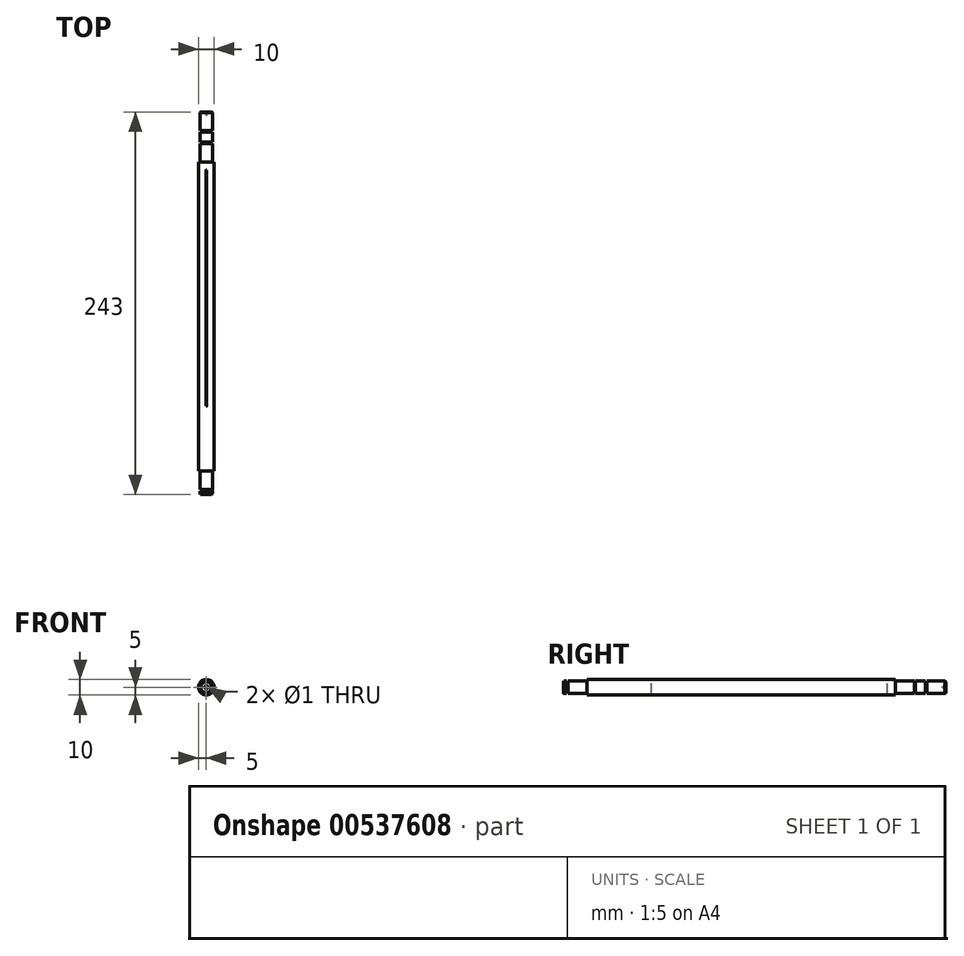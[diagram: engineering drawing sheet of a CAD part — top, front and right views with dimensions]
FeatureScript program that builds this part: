
annotation { "Feature Type Name" : "Feature", "Feature Type Description" : "" }
export const myFeature = defineFeature(function(context is Context, id is Id, definition is map)
    precondition{}
    {
        {
            var Q0;
            Q0=qCreatedBy(makeId("Front.planeOp"),FACE);
            var sketch = newSketch(context, id + "F0", { "sketchPlane" : qUnion([Q0])});
            skCircle(sketch, "E0", {"center": v(0, 0) * mm, "radius": 5 * mm});
            skSolve(sketch);
        }
        {
            var Q0;
            Q0=makeQuery(id+"F0.imprint","IMPRINT",FACE,{"disambiguationData":[TD([[makeQuery(id+"F0.imprint","IMPRINT",EDGE,{"derivedFrom":sQuery(id+"F0.wireOp",EDGE,"E0")}),1.0]])]});
            extrude(context, id + "F1", {"entities" : qUnion([Q0]), "flatOperationType" : FlatOperationType.REMOVE, "depth" : 220 * mm, "offsetDistance" : 25 * mm, "domain" : OperationDomain.MODEL});
        }
        {
            var Q0;
            Q0=qCreatedBy(makeId("Right.planeOp"),FACE);
            var sketch = newSketch(context, id + "F2", { "sketchPlane" : qUnion([Q0])});
            skLineSegment(sketch, "E1", {"start": v(0, 5) * mm, "end": v(-12, 5) * mm});
            skLineSegment(sketch, "E2", {"start": v(-12, 5) * mm, "end": v(-12, 4) * mm});
            skLineSegment(sketch, "E3", {"start": v(-12, 4) * mm, "end": v(0, 4) * mm});
            skLineSegment(sketch, "E4", {"start": v(0, 4) * mm, "end": v(0, 5) * mm});
            skLineSegment(sketch, "E5", {"start": v(-220, 5) * mm, "end": v(-208, 5) * mm});
            skLineSegment(sketch, "E6", {"start": v(-208, 5) * mm, "end": v(-208, 4) * mm});
            skLineSegment(sketch, "E7", {"start": v(-208, 4) * mm, "end": v(-220, 4) * mm});
            skLineSegment(sketch, "E8", {"start": v(-220, 4) * mm, "end": v(-220, 5) * mm});
            skSolve(sketch);
        }
        {
            var Q0;
            Q0 = qSketchRegion(id + "F2", true);
            var Q1;
            Q1=makeQuery(id+"F1.opExtrude","SWEPT_FACE",FACE,{"disambiguationData":[OSD([sQuery(id+"F0.wireOp",EDGE,"E0")])]});
            revolve(context, id + "F3", {"operationType" : NewBodyOperationType.REMOVE, "entities" : qUnion([Q0]), "axis" : qUnion([Q1]), "revolveType" : RevolveType.FULL, "oppositeDirection" : true});
        }
        {
            var Q0;
            Q0=qCreatedBy(makeId("Top.planeOp"),FACE);
            var sketch = newSketch(context, id + "F4", { "sketchPlane" : qUnion([Q0])});
            skLineSegment(sketch, "E9.bottom", {"start": v(0.3, -17) * mm, "end": v(-0.3, -17) * mm});
            skLineSegment(sketch, "E9.top", {"start": v(0.3, -167) * mm, "end": v(-0.3, -167) * mm});
            skLineSegment(sketch, "E9.left", {"start": v(0.3, -17) * mm, "end": v(0.3, -167) * mm});
            skLineSegment(sketch, "E9.right", {"start": v(-0.3, -17) * mm, "end": v(-0.3, -167) * mm});
            skSolve(sketch);
        }
        {
            var Q0;
            Q0 = qSketchRegion(id + "F4", true);
            extrude(context, id + "F5", {"entities" : qUnion([Q0]), "operationType" : NewBodyOperationType.REMOVE, "oppositeDirection" : true, "depth" : 25 * mm, "offsetDistance" : 25 * mm, "symmetric" : true});
        }
        {
            var Q0;
            Q0=makeQuery(id+"F1.opExtrude","CAP_FACE",FACE,{"disambiguationData":[OSD([sQuery(id+"F0.wireOp",EDGE,"E0")])],"isStart":false});
            extrude(context, id + "F6", {"entities" : qUnion([Q0]), "operationType" : NewBodyOperationType.ADD, "depth" : 3 * mm, "offsetDistance" : 25 * mm});
        }
        {
            var Q0;
            Q0=makeQuery(id+"F1.opExtrude","CAP_FACE",FACE,{"disambiguationData":[OSD([sQuery(id+"F0.wireOp",EDGE,"E0")])],"isStart":true});
            extrude(context, id + "F7", {"entities" : qUnion([Q0]), "operationType" : NewBodyOperationType.ADD, "depth" : 20 * mm, "offsetDistance" : 25 * mm});
        }
        {
            var Q0;
            Q0=qCreatedBy(makeId("Right.planeOp"),FACE);
            var sketch = newSketch(context, id + "F8", { "sketchPlane" : qUnion([Q0])});
            skLineSegment(sketch, "E10", {"start": v(0, 4) * mm, "end": v(0, 3) * mm});
            skLineSegment(sketch, "E11", {"start": v(0, 3) * mm, "end": v(0.8, 3) * mm});
            skLineSegment(sketch, "E12", {"start": v(0.8, 3) * mm, "end": v(0.8, 4) * mm});
            skLineSegment(sketch, "E13", {"start": v(0.8, 4) * mm, "end": v(0, 4) * mm});
            skLineSegment(sketch, "E14.bottom", {"start": v(-220.8, 4) * mm, "end": v(-220, 4) * mm});
            skLineSegment(sketch, "E14.top", {"start": v(-220.8, 3) * mm, "end": v(-220, 3) * mm});
            skLineSegment(sketch, "E14.left", {"start": v(-220.8, 4) * mm, "end": v(-220.8, 3) * mm});
            skLineSegment(sketch, "E14.right", {"start": v(-220, 4) * mm, "end": v(-220, 3) * mm});
            skLineSegment(sketch, "E15", {"start": v(0, 0) * mm, "end": v(-212.78, 0) * mm});
            skLineSegment(sketch, "E16", {"start": v(7, 3) * mm, "end": v(8, 3) * mm});
            skLineSegment(sketch, "E17", {"start": v(8, 3) * mm, "end": v(8, 4) * mm});
            skLineSegment(sketch, "E18", {"start": v(8, 4) * mm, "end": v(7, 4) * mm});
            skLineSegment(sketch, "E19", {"start": v(7, 4) * mm, "end": v(7, 3) * mm});
            skSolve(sketch);
        }
        {
            var Q0;
            Q0 = qSketchRegion(id + "F8", true);
            var Q1;
            Q1=sQuery(id+"F8.wireOp",EDGE,"E15");
            revolve(context, id + "F9", {"operationType" : NewBodyOperationType.REMOVE, "entities" : qUnion([Q0]), "axis" : qUnion([Q1]), "revolveType" : RevolveType.FULL, "oppositeDirection" : true});
        }
        {
            var Q0;
            Q0=makeQuery(id+"F6.opExtrude","CAP_EDGE",EDGE,{"disambiguationData":[OSD([sQuery(id+"F2.wireOp",EDGE,"E7"),sQuery(id+"F2.wireOp",EDGE,"E8")])],"isStart":false});
            var Q1;
            Q1=makeQuery(id+"F3.boolean.opBoolean","COPY",EDGE,{"derivedFrom":makeQuery(id+"F3.opRevolve","SWEPT_EDGE",EDGE,{"disambiguationData":[OSD([sQuery(id+"F2.wireOp",EDGE,"E5"),sQuery(id+"F2.wireOp",EDGE,"E6")])]})});
            var Q2;
            Q2=makeQuery(id+"F3.boolean.opBoolean","COPY",EDGE,{"derivedFrom":makeQuery(id+"F3.opRevolve","SWEPT_EDGE",EDGE,{"disambiguationData":[OSD([sQuery(id+"F2.wireOp",EDGE,"E1"),sQuery(id+"F2.wireOp",EDGE,"E2")])]})});
            var Q3;
            Q3=makeQuery(id+"F9.boolean.opBoolean","COPY",EDGE,{"derivedFrom":makeQuery(id+"F9.opRevolve","SWEPT_EDGE",EDGE,{"disambiguationData":[OSD([sQuery(id+"F8.wireOp",EDGE,"E17"),sQuery(id+"F8.wireOp",EDGE,"E18")])]})});
            var Q4;
            Q4=makeQuery(id+"F7.opExtrude","CAP_EDGE",EDGE,{"disambiguationData":[OSD([sQuery(id+"F2.wireOp",EDGE,"E3"),sQuery(id+"F2.wireOp",EDGE,"E4")])],"isStart":false});
            chamfer(context, id + "F10", {"entities" : qUnion([Q0, Q1, Q2, Q3, Q4]), "width" : .5 * mm, "tangentPropagation" : true});
        }
        {
            var Q0;
            Q0=makeQuery(id+"F7.opExtrude","CAP_FACE",FACE,{"disambiguationData":[OSD([sQuery(id+"F0.wireOp",EDGE,"E0")])],"isStart":false});
            var sketch = newSketch(context, id + "F11", { "sketchPlane" : qUnion([Q0])});
            skPoint(sketch, "E20", {"position": v(0, 0) * mm});
            skSolve(sketch);
        }
        {
            var Q0;
            Q0=makeQuery(id+"F6.opExtrude","CAP_FACE",FACE,{"disambiguationData":[OSD([sQuery(id+"F0.wireOp",EDGE,"E0")])],"isStart":false});
            var sketch = newSketch(context, id + "F12", { "sketchPlane" : qUnion([Q0])});
            skPoint(sketch, "E21", {"position": v(0, 0) * mm});
            skSolve(sketch);
        }
        {
            var Q0;
            Q0=sQuery(id+"F12.wireOp",VERTEX,"E21");
            var Q1;
            Q1=sQuery(id+"F11.wireOp",VERTEX,"E20");
            var Q2;
            Q2=makeQuery(id+"F1.opExtrude","SWEPT_BODY",BODY,{"disambiguationData":[OSD([sQuery(id+"F0.wireOp",EDGE,"E0")])]});
            hole(context, id + "F13", {"style" : HoleStyle.C_SINK, "endStyle" : HoleEndStyle.BLIND, "holeDiameter" : 1 * mm, "cSinkDiameter" : 2.12 * mm, "cSinkAngle" : 60 * degree, "holeDepth" : 1.9 * mm, "isTappedThrough" : true, "tappedDepth" : 12 * mm, "tapClearance" : 3, "locations" : qUnion([Q0, Q1]), "scope" : qUnion([Q2])});
        }
    });
